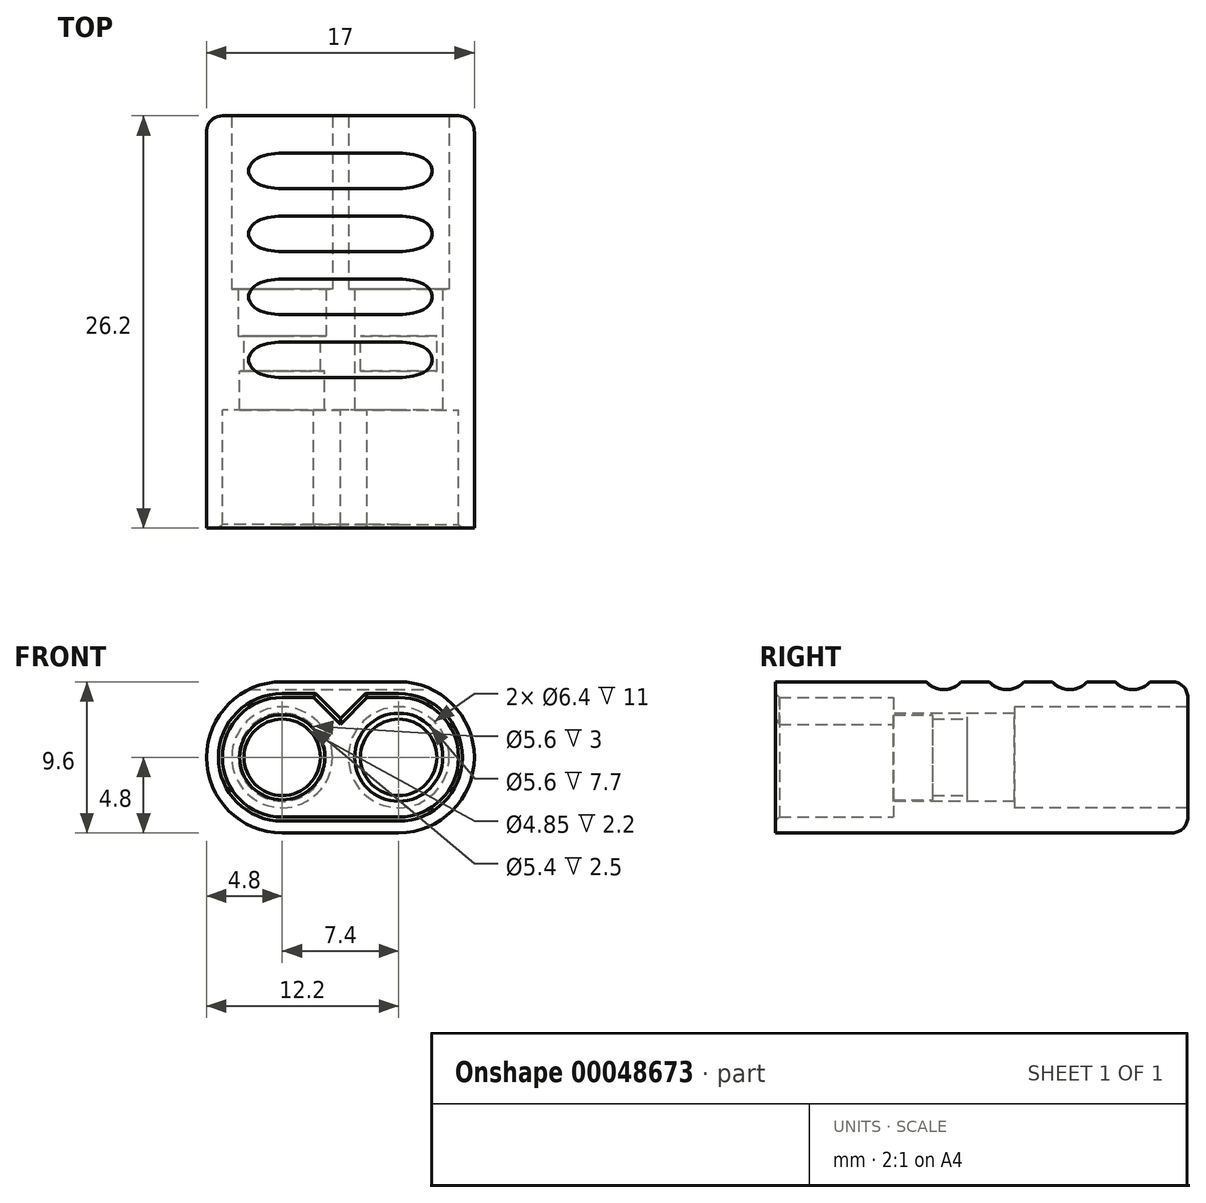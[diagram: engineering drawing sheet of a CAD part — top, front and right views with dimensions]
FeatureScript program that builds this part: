
annotation { "Feature Type Name" : "Feature", "Feature Type Description" : "" }
export const myFeature = defineFeature(function(context is Context, id is Id, definition is map)
    precondition{}
    {
        {
            var Q0;
            Q0=qCreatedBy(makeId("Front.planeOp"),FACE);
            var sketch = newSketch(context, id + "F0", { "sketchPlane" : qUnion([Q0])});
            skCircle(sketch, "E0", {"center": v(-3.7, 0) * mm, "radius": 2.43 * mm});
            skCircle(sketch, "E1.MirrorC", {"center": v(-3.7, 0) * mm, "radius": 2.8 * mm});
            skLineSegment(sketch, "E2", {"start": v(0, 0) * mm, "end": v(-8.5, 0) * mm, "construction": true});
            skArc(sketch, "E3", {"start": v(-3.7, 4.8) * mm, "mid": v(-7.1, 3.4) * mm, "end": v(-8.5, 0) * mm});
            skLineSegment(sketch, "E4", {"start": v(0, 4.8) * mm, "end": v(0, 0) * mm, "construction": true});
            skLineSegment(sketch, "E5", {"start": v(-3.7, 4.8) * mm, "end": v(-3.7, 0) * mm, "construction": true});
            skCircle(sketch, "E6.MirrorC", {"center": v(3.7, 0) * mm, "radius": 2.43 * mm});
            skCircle(sketch, "E7.MirrorC", {"center": v(3.7, 0) * mm, "radius": 2.8 * mm});
            skLineSegment(sketch, "E8", {"start": v(-3.7, 4.8) * mm, "end": v(0, 4.8) * mm});
            skArc(sketch, "E9.MirrorCS", {"start": v(-3.7, -4.8) * mm, "mid": v(-7.1, -3.4) * mm, "end": v(-8.5, 0) * mm});
            skLineSegment(sketch, "E10.MirrorCS", {"start": v(-3.7, -4.8) * mm, "end": v(0, -4.8) * mm});
            skLineSegment(sketch, "E11.MirrorCS", {"start": v(3.7, 4.8) * mm, "end": v(0, 4.8) * mm});
            skArc(sketch, "E12.MirrorCS", {"start": v(3.7, 4.8) * mm, "mid": v(7.1, 3.4) * mm, "end": v(8.5, 0) * mm});
            skArc(sketch, "E13.MirrorCS", {"start": v(3.7, -4.8) * mm, "mid": v(7.1, -3.4) * mm, "end": v(8.5, 0) * mm});
            skLineSegment(sketch, "E14.MirrorCS", {"start": v(3.7, -4.8) * mm, "end": v(0, -4.8) * mm});
            skSolve(sketch);
        }
        {
            var Q0;
            Q0=makeQuery(id+"F0.imprint","IMPRINT",FACE,{"disambiguationData":[TD([[makeQuery(id+"F0.imprint","IMPRINT",EDGE,{"derivedFrom":sQuery(id+"F0.wireOp",EDGE,"E1.MirrorC")}),-1.0]])]});
            extrude(context, id + "F1", {"entities" : qUnion([Q0]), "oppositeDirection" : true, "depth" : 3 * mm});
        }
        {
            var Q0;
            Q0=makeQuery(id+"F0.imprint","IMPRINT",FACE,{"disambiguationData":[TD([[makeQuery(id+"F0.imprint","IMPRINT",EDGE,{"derivedFrom":sQuery(id+"F0.wireOp",EDGE,"E1.MirrorC")}),-1.0]])]});
            var Q1;
            Q1=makeQuery(id+"F0.imprint","IMPRINT",FACE,{"disambiguationData":[TD([[makeQuery(id+"F0.imprint","IMPRINT",EDGE,{"derivedFrom":sQuery(id+"F0.wireOp",EDGE,"E0")}),-1.0]])]});
            var Q2;
            Q2=makeQuery(id+"F0.imprint","IMPRINT",FACE,{"disambiguationData":[TD([[makeQuery(id+"F0.imprint","IMPRINT",EDGE,{"derivedFrom":sQuery(id+"F0.wireOp",EDGE,"E6.MirrorC")}),1.0]])]});
            extrude(context, id + "F2", {"entities" : qUnion([Q0, Q1, Q2]), "operationType" : NewBodyOperationType.ADD, "depth" : 2.2 * mm});
        }
        {
            var Q0;
            Q0=makeQuery(id+"F2.opExtrude","CAP_FACE",FACE,{"disambiguationData":[OSD([sQuery(id+"F0.wireOp",EDGE,"9af29b95-2ce9-48ef-83fd-eb93086e848a.bottom"),sQuery(id+"F0.wireOp",EDGE,"9af29b95-2ce9-48ef-83fd-eb93086e848a.top"),sQuery(id+"F0.wireOp",EDGE,"9af29b95-2ce9-48ef-83fd-eb93086e848a.left"),sQuery(id+"F0.wireOp",EDGE,"9af29b95-2ce9-48ef-83fd-eb93086e848a.right"),sQuery(id+"F0.wireOp",EDGE,"E0"),sQuery(id+"F0.wireOp",EDGE,"3bfeefd6-8ccf-4d28-93f8-2f2611132b7e0.MirrorC")])],"isStart":false});
            var sketch = newSketch(context, id + "F3", { "sketchPlane" : qUnion([Q0])});
            skCircle(sketch, "E15", {"center": v(-3.7, 0) * mm, "radius": 2.7 * mm});
            skCircle(sketch, "E16.MirrorC", {"center": v(3.7, 0) * mm, "radius": 2.7 * mm});
            skSolve(sketch);
        }
        {
            var Q0;
            Q0=makeQuery(id+"F3.imprint","IMPRINT",FACE,{"disambiguationData":[TD([[makeQuery(id+"F3.imprint","IMPRINT",EDGE,{"derivedFrom":sQuery(id+"F3.wireOp",EDGE,"E15")}),-1.0]])]});
            extrude(context, id + "F4", {"entities" : qUnion([Q0]), "operationType" : NewBodyOperationType.ADD, "depth" : 2.5 * mm});
        }
        {
            var Q0;
            Q0=makeQuery(id+"F4.opExtrude","CAP_FACE",FACE,{"disambiguationData":[OSD([sQuery(id+"F0.wireOp",EDGE,"6d7ef5f6-68e2-491c-bdb9-d34946de3217"),sQuery(id+"F0.wireOp",EDGE,"4a62e17a-e464-4ae6-85fd-e67879230d62"),sQuery(id+"F0.wireOp",EDGE,"d8da9cf0-fa24-4876-8edd-ab64fd6ac28d"),sQuery(id+"F0.wireOp",EDGE,"6ed2982d-5885-44c9-aeb3-c63c06cbabe1.filletArc"),sQuery(id+"F0.wireOp",EDGE,"ac0d3ca8-c71e-4b4c-905e-2867e2134c0f.filletArc"),sQuery(id+"F0.wireOp",EDGE,"db059e13-4987-40d7-b22c-4aa99c86301e0.MirrorCS"),sQuery(id+"F0.wireOp",EDGE,"21968229-6fcb-4818-9fba-464d6f3a7a490.MirrorCS"),sQuery(id+"F0.wireOp",EDGE,"27c3a9c7-bba5-4ce6-a0b2-ee3fde2fc81d0.MirrorCS"),sQuery(id+"F0.wireOp",EDGE,"74e78b0a-03c2-4682-ad69-f2b08288fff30.MirrorCS"),sQuery(id+"F0.wireOp",EDGE,"d6014dcf-48b1-47f5-9b02-8fcda7855cd30.MirrorCS"),sQuery(id+"F3.wireOp",EDGE,"E15"),sQuery(id+"F3.wireOp",EDGE,"3893830b-eff6-4bac-9637-d990255e7b810.MirrorC")])],"isStart":false});
            var sketch = newSketch(context, id + "F5", { "sketchPlane" : qUnion([Q0])});
            skLineSegment(sketch, "E17", {"start": v(-3.7, -3.8) * mm, "end": v(0, -3.8) * mm});
            skLineSegment(sketch, "E18", {"start": v(-1.7, 3.8) * mm, "end": v(0, 2.1) * mm});
            skArc(sketch, "E19", {"start": v(-3.7, 3.8) * mm, "mid": v(-7.5, 0) * mm, "end": v(-3.7, -3.8) * mm});
            skLineSegment(sketch, "E20", {"start": v(-3.7, 3.8) * mm, "end": v(-1.7, 3.8) * mm});
            skLineSegment(sketch, "E21.MirrorCS", {"start": v(1.7, 3.8) * mm, "end": v(0, 2.1) * mm});
            skLineSegment(sketch, "E22.MirrorCS", {"start": v(3.7, 3.8) * mm, "end": v(1.7, 3.8) * mm});
            skArc(sketch, "E23.MirrorCS", {"start": v(3.7, 3.8) * mm, "mid": v(7.5, 0) * mm, "end": v(3.7, -3.8) * mm});
            skLineSegment(sketch, "E24.MirrorCS", {"start": v(3.7, -3.8) * mm, "end": v(0, -3.8) * mm});
            skSolve(sketch);
        }
        {
            var Q0;
            Q0=makeQuery(id+"F5.imprint","IMPRINT",FACE,{"disambiguationData":[TD([[makeQuery(id+"F5.imprint","IMPRINT",EDGE,{"derivedFrom":sQuery(id+"F5.wireOp",EDGE,"E17")}),-1.0]])]});
            extrude(context, id + "F6", {"entities" : qUnion([Q0]), "operationType" : NewBodyOperationType.ADD, "depth" : 7.5 * mm});
        }
        {
            var Q0;
            Q0=makeQuery(id+"F1.opExtrude","CAP_FACE",FACE,{"disambiguationData":[OSD([sQuery(id+"F0.wireOp",EDGE,"E1.MirrorC"),sQuery(id+"F0.wireOp",EDGE,"E3"),sQuery(id+"F0.wireOp",EDGE,"E7.MirrorC"),sQuery(id+"F0.wireOp",EDGE,"E8"),sQuery(id+"F0.wireOp",EDGE,"E9.MirrorCS"),sQuery(id+"F0.wireOp",EDGE,"E10.MirrorCS"),sQuery(id+"F0.wireOp",EDGE,"E11.MirrorCS"),sQuery(id+"F0.wireOp",EDGE,"E12.MirrorCS"),sQuery(id+"F0.wireOp",EDGE,"E13.MirrorCS"),sQuery(id+"F0.wireOp",EDGE,"E14.MirrorCS")])],"isStart":false});
            var sketch = newSketch(context, id + "F7", { "sketchPlane" : qUnion([Q0])});
            skCircle(sketch, "E25", {"center": v(3.7, 0) * mm, "radius": 3.2 * mm});
            skCircle(sketch, "E26.MirrorC", {"center": v(-3.7, 0) * mm, "radius": 3.2 * mm});
            skSolve(sketch);
        }
        {
            var Q0;
            Q0=makeQuery(id+"F7.imprint","IMPRINT",FACE,{"disambiguationData":[TD([[makeQuery(id+"F7.imprint","IMPRINT",EDGE,{"derivedFrom":sQuery(id+"F7.wireOp",EDGE,"E25")}),-1.0]])]});
            extrude(context, id + "F8", {"entities" : qUnion([Q0]), "operationType" : NewBodyOperationType.ADD, "depth" : 11 * mm});
        }
        {
            var Q0;
            Q0=makeQuery(id+"F8.opExtrude","CAP_EDGE",EDGE,{"disambiguationData":[OSD([sQuery(id+"F0.wireOp",EDGE,"E8"),sQuery(id+"F0.wireOp",EDGE,"E11.MirrorCS")])],"isStart":false});
            fillet(context, id + "F9", {"entities" : qUnion([Q0]), "radius" : 1 * mm, "tangentPropagation" : true, "allowEdgeOverflow" : false});
        }
        {
            var Q0;
            Q0=makeQuery(id+"F6.opExtrude","CAP_EDGE",EDGE,{"disambiguationData":[OSD([sQuery(id+"F5.wireOp",EDGE,"E19")])],"isStart":false});
            var Q1;
            Q1=makeQuery(id+"F6.opExtrude","CAP_EDGE",EDGE,{"disambiguationData":[OSD([sQuery(id+"F5.wireOp",EDGE,"E20")])],"isStart":false});
            var Q2;
            Q2=makeQuery(id+"F6.opExtrude","CAP_EDGE",EDGE,{"disambiguationData":[OSD([sQuery(id+"F5.wireOp",EDGE,"E18")])],"isStart":false});
            var Q3;
            Q3=makeQuery(id+"F6.opExtrude","CAP_EDGE",EDGE,{"disambiguationData":[OSD([sQuery(id+"F5.wireOp",EDGE,"E21.MirrorCS")])],"isStart":false});
            var Q4;
            Q4=makeQuery(id+"F6.opExtrude","CAP_EDGE",EDGE,{"disambiguationData":[OSD([sQuery(id+"F5.wireOp",EDGE,"E22.MirrorCS")])],"isStart":false});
            var Q5;
            Q5=makeQuery(id+"F6.opExtrude","CAP_EDGE",EDGE,{"disambiguationData":[OSD([sQuery(id+"F5.wireOp",EDGE,"E23.MirrorCS")])],"isStart":false});
            var Q6;
            Q6=makeQuery(id+"F6.opExtrude","CAP_EDGE",EDGE,{"disambiguationData":[OSD([sQuery(id+"F5.wireOp",EDGE,"E17"),sQuery(id+"F5.wireOp",EDGE,"E24.MirrorCS")])],"isStart":false});
            chamfer(context, id + "F10", {"entities" : qUnion([Q0, Q1, Q2, Q3, Q4, Q5, Q6]), "width" : 0.25 * mm, "tangentPropagation" : true});
        }
        {
            var Q0;
            Q0=qCreatedBy(makeId("Right.planeOp"),FACE);
            var sketch = newSketch(context, id + "F11", { "sketchPlane" : qUnion([Q0])});
            skCircle(sketch, "E27", {"center": v(2.5, 5.8) * mm, "radius": 1.5 * mm});
            skCircle(sketch, "E28", {"center": v(10.5, 5.8) * mm, "radius": 1.5 * mm});
            skLineSegment(sketch, "E29", {"start": v(14.5, 0) * mm, "end": v(-12.5, 0) * mm, "construction": true});
            skCircle(sketch, "E30", {"center": v(6.5, 5.8) * mm, "radius": 1.5 * mm});
            skCircle(sketch, "E31.MirrorC", {"center": v(6.5, -5.8) * mm, "radius": 1.5 * mm});
            skCircle(sketch, "E32.MirrorC", {"center": v(2.5, -5.8) * mm, "radius": 1.5 * mm});
            skCircle(sketch, "E33.MirrorC", {"center": v(10.5, -5.8) * mm, "radius": 1.5 * mm});
            skLineSegment(sketch, "E34", {"start": v(10.5, 5.8) * mm, "end": v(-1.5, 5.8) * mm, "construction": true});
            skCircle(sketch, "E35", {"center": v(-1.5, 5.8) * mm, "radius": 1.5 * mm});
            skCircle(sketch, "E36.MirrorC", {"center": v(-1.5, -5.8) * mm, "radius": 1.5 * mm});
            skSolve(sketch);
        }
        {
            var Q0;
            Q0=makeQuery(id+"F11.imprint","IMPRINT",FACE,{"disambiguationData":[TD([[makeQuery(id+"F11.imprint","IMPRINT",EDGE,{"derivedFrom":sQuery(id+"F11.wireOp",EDGE,"E27")}),1.0]])]});
            var Q1;
            Q1=makeQuery(id+"F11.imprint","IMPRINT",FACE,{"disambiguationData":[TD([[makeQuery(id+"F11.imprint","IMPRINT",EDGE,{"derivedFrom":sQuery(id+"F11.wireOp",EDGE,"E30")}),1.0]])]});
            var Q2;
            Q2=makeQuery(id+"F11.imprint","IMPRINT",FACE,{"disambiguationData":[TD([[makeQuery(id+"F11.imprint","IMPRINT",EDGE,{"derivedFrom":sQuery(id+"F11.wireOp",EDGE,"E28")}),1.0]])]});
            var Q3;
            Q3=makeQuery(id+"F11.imprint","IMPRINT",FACE,{"disambiguationData":[TD([[makeQuery(id+"F11.imprint","IMPRINT",EDGE,{"derivedFrom":sQuery(id+"F11.wireOp",EDGE,"E32.MirrorC")}),-1.0]])]});
            var Q4;
            Q4=makeQuery(id+"F11.imprint","IMPRINT",FACE,{"disambiguationData":[TD([[makeQuery(id+"F11.imprint","IMPRINT",EDGE,{"derivedFrom":sQuery(id+"F11.wireOp",EDGE,"E31.MirrorC")}),-1.0]])]});
            var Q5;
            Q5=makeQuery(id+"F11.imprint","IMPRINT",FACE,{"disambiguationData":[TD([[makeQuery(id+"F11.imprint","IMPRINT",EDGE,{"derivedFrom":sQuery(id+"F11.wireOp",EDGE,"E33.MirrorC")}),-1.0]])]});
            var Q6;
            Q6=makeQuery(id+"F11.imprint","IMPRINT",FACE,{"disambiguationData":[TD([[makeQuery(id+"F11.imprint","IMPRINT",EDGE,{"derivedFrom":sQuery(id+"F11.wireOp",EDGE,"E35")}),1.0]])]});
            var Q7;
            Q7=makeQuery(id+"F11.imprint","IMPRINT",FACE,{"disambiguationData":[TD([[makeQuery(id+"F11.imprint","IMPRINT",EDGE,{"derivedFrom":sQuery(id+"F11.wireOp",EDGE,"E36.MirrorC")}),-1.0]])]});
            extrude(context, id + "F12", {"entities" : qUnion([Q0, Q1, Q2, Q3, Q4, Q5, Q6, Q7]), "operationType" : NewBodyOperationType.REMOVE, "endBound" : BoundingType.SYMMETRIC, "oppositeDirection" : true, "depth" : 17 * mm});
        }
    });
